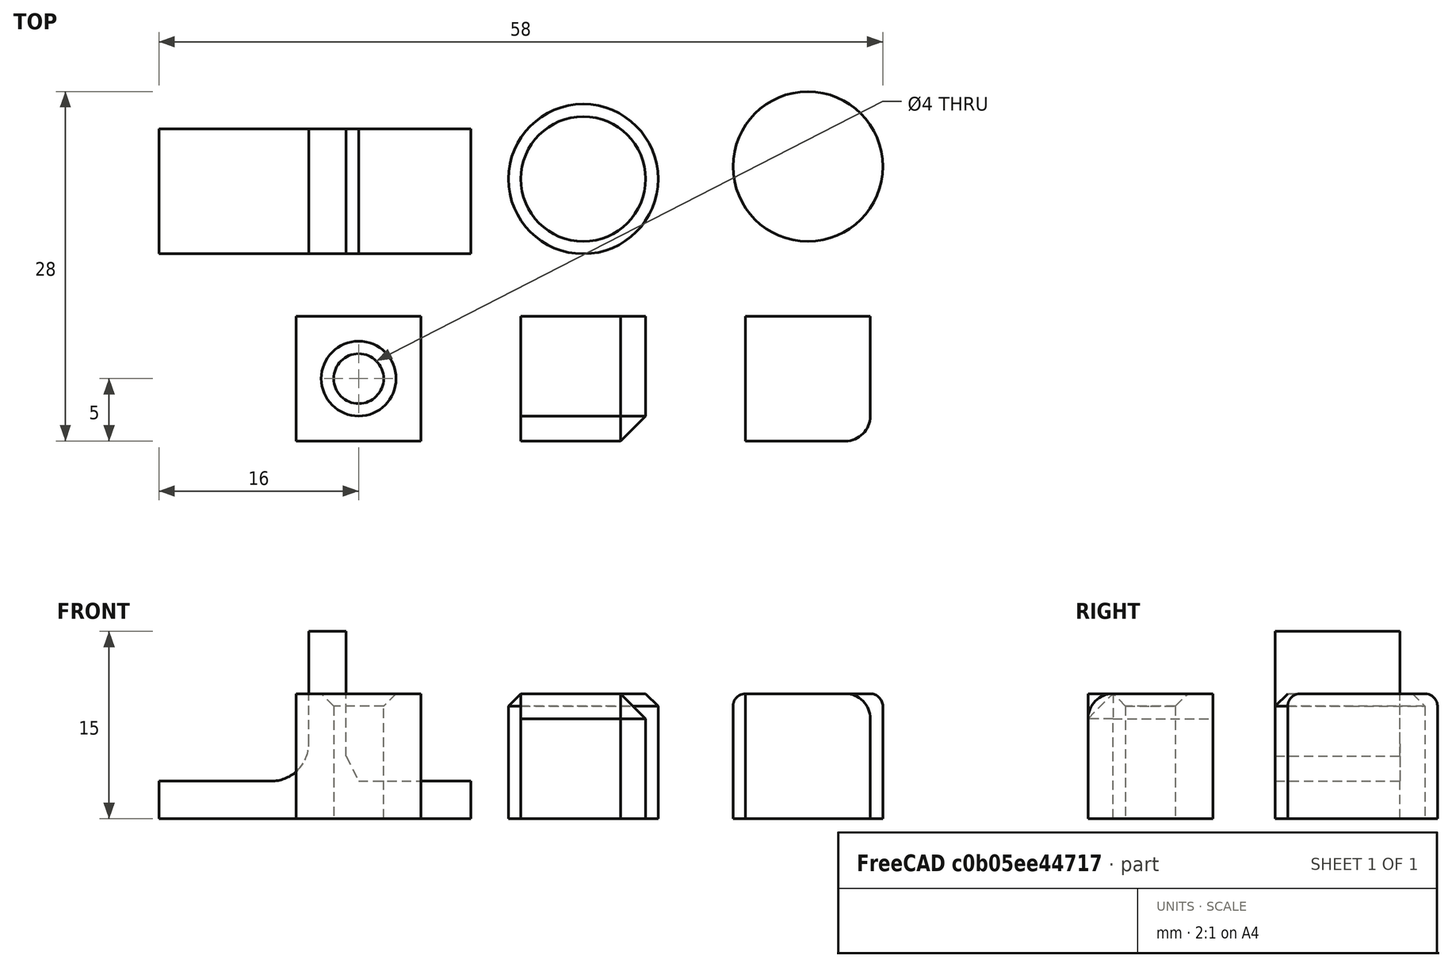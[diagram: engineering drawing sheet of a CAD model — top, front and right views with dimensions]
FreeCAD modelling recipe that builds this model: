
FCSTD DOCUMENT  (FreeCAD 0.21R33694 (Git))
Label: OJT1_T12P01_arrodoniments_xamfrans_reforços
License: All rights reserved
LicenseURL: https://en.wikipedia.org/wiki/All_rights_reserved
objects: Part::Box×5, Part::Chamfer×4, Part::Fillet×3, Part::Cylinder×3, Part::Cut×1, Part::MultiFuse×1, Part::Refine×1
note: 18 computed .brp shape members not serialized (recipe doc carries the construction recipe); baked Part::Feature solids carry a one-line shape summary decoded from their .brp

FEATURE [Part::Box] Box  label="Cub"
  AttacherType = Attacher::AttachEngine3D
  Height = 10
  Length = 10
  Width = 10
FEATURE [Part::Fillet] Fillet  label="Cub_1"
  Base = -> Box
  Edges = 3 edges r=2: [Edge5,Edge6,Edge10]
FEATURE [Part::Box] Box001  label="Cub001"
  AttacherType = Attacher::AttachEngine3D
  Height = 10
  Length = 10
  Placement = pos=(-18,0,0) rot=(0,0,1;0rad)
  Width = 10
FEATURE [Part::Chamfer] Chamfer  label="Cub_2"
  Base = -> Box001
  Edges = 3 edges r=2: [Edge5,Edge6,Edge10]
FEATURE [Part::Box] Box002  label="Cub002"
  AttacherType = Attacher::AttachEngine3D
  Height = 10
  Length = 10
  Placement = pos=(-36,0,0) rot=(0,0,1;0rad)
  Width = 10
FEATURE [Part::Cylinder] Cylinder  label="Cilindre"
  Angle = 360
  AttacherType = Attacher::AttachEngine3D
  FirstAngle = 0
  Height = 10
  Placement = pos=(-31,5,0) rot=(0,0,1;0rad)
  Radius = 2
  SecondAngle = 0
FEATURE [Part::Cut] Cut  label="Cub_forat"
  Base = -> Box002
  Tool = -> Cylinder
FEATURE [Part::Chamfer] Chamfer001  label="Cub_3"
  Base = -> Cut
  Edges = 1 edges r=1: [Edge10]
FEATURE [Part::Cylinder] Cylinder001  label="Cilindre001"
  Angle = 360
  AttacherType = Attacher::AttachEngine3D
  FirstAngle = 0
  Height = 10
  Placement = pos=(5,22,0) rot=(0,0,1;0rad)
  Radius = 6
  SecondAngle = 0
FEATURE [Part::Fillet] Fillet001  label="Cilindre_1"
  Base = -> Cylinder001
  Edges = 1 edges r=1: [Edge3]
FEATURE [Part::Cylinder] Cylinder002  label="Cilindre002"
  Angle = 360
  AttacherType = Attacher::AttachEngine3D
  FirstAngle = 0
  Height = 10
  Placement = pos=(-13,21,0) rot=(0,0,1;0rad)
  Radius = 6
  SecondAngle = 0
FEATURE [Part::Chamfer] Chamfer002
  Base = -> Cylinder002
  Edges = 1 edges r=1: [Edge3]
FEATURE [Part::Box] Box003  label="Cub003"
  AttacherType = Attacher::AttachEngine3D
  Height = 3
  Length = 25
  Placement = pos=(-47,15,0) rot=(0,0,1;0rad)
  Width = 10
FEATURE [Part::Box] Box004  label="Cub004"
  AttacherType = Attacher::AttachEngine3D
  Height = 15
  Length = 3
  Placement = pos=(-35,15,0) rot=(0,0,1;0rad)
  Width = 10
FEATURE [Part::MultiFuse] Fusion
  Shapes = -> [Box003,Box004]
FEATURE [Part::Refine] Fusion001  label="Doble rampa"
  Source = -> Fusion
FEATURE [Part::Chamfer] Chamfer003
  Base = -> Fusion001
  Edges = 1 edges: [Edge16 r1=2 r2=1]
FEATURE [Part::Fillet] Fillet002
  Base = -> Chamfer003
  Edges = 1 edges r=3: [Edge27]
